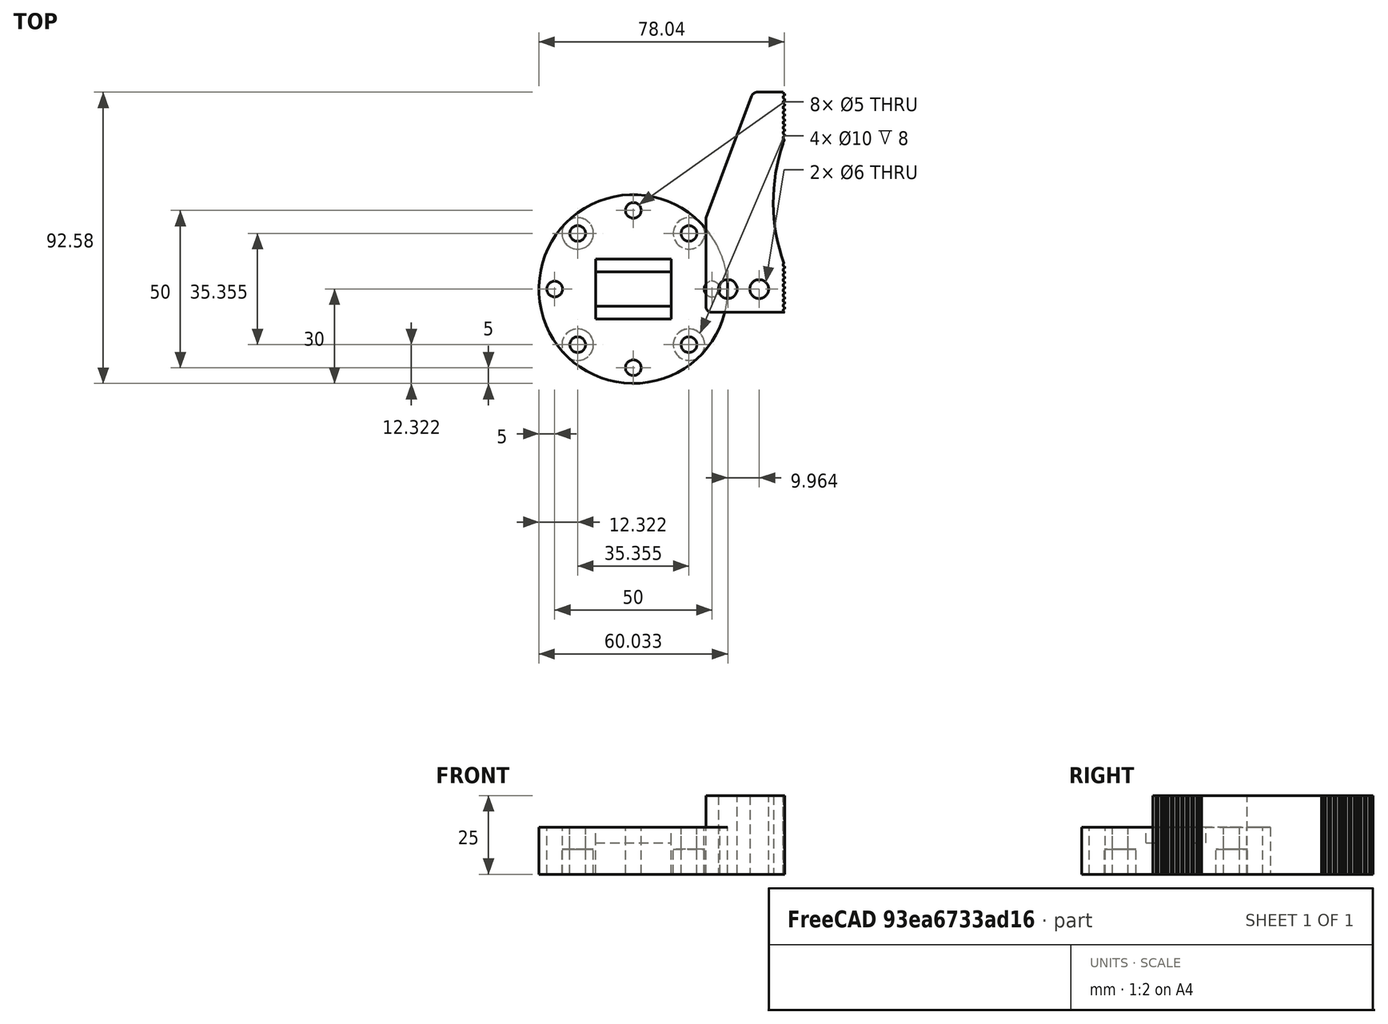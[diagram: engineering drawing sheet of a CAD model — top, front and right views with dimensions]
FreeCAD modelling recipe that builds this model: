
FCSTD DOCUMENT  (FreeCAD 0.16R6712 (Git))
Label: Garra
License: All rights reserved
LicenseURL: http://en.wikipedia.org/wiki/All_rights_reserved
objects: Part::Cylinder×5, Part::FeaturePython×5, Part::Cut×4, Sketcher::SketchObject×3, App::DocumentObjectGroup×3, PartDesign::Pad×2, Part::Fillet×2, Part::Box×1
note: 24 computed .brp shape members not serialized (recipe doc carries the construction recipe); baked Part::Feature solids carry a one-line shape summary decoded from their .brp

FEATURE [Sketcher::SketchObject] Sketch
  sketch-geometry (9):
    g0: LineSegment StartX=23.0433 StartY=-7.41801 StartZ=0 EndX=48.0433 EndY=-7.41801 EndZ=0
    g1: LineSegment StartX=23.0433 StartY=-7.41801 StartZ=0 EndX=23.0433 EndY=22.582 EndZ=0
    g2: LineSegment StartX=48.0433 StartY=-7.41801 StartZ=0 EndX=48.0433 EndY=7.58199 EndZ=0
    g3: LineSegment StartX=23.0433 StartY=22.582 StartZ=0 EndX=38.0433 EndY=62.582 EndZ=0
    g4: LineSegment StartX=38.0433 StartY=62.582 StartZ=0 EndX=48.0433 EndY=62.582 EndZ=0
    g5: LineSegment StartX=48.0433 StartY=62.582 StartZ=0 EndX=48.0433 EndY=47.582 EndZ=0
    g6: ArcOfCircle CenterX=102.486 CenterY=27.582 CenterZ=0 NormalX=0 NormalY=0 NormalZ=1 Radius=58 StartAngle=2.78954 EndAngle=3.49365
    g7: Circle CenterX=30.0326 CenterY=0 CenterZ=0 NormalX=0 NormalY=0 NormalZ=1 Radius=3
    g8: Circle CenterX=39.997 CenterY=0 CenterZ=0 NormalX=0 NormalY=0 NormalZ=1 Radius=3
  constraints (24):
    c: Horizontal(g0)
    c: Coincident(g1,g0)
    c: Vertical(g1)
    c: Coincident(g2,g0)
    c: Vertical(g2)
    c: DistanceY(g1,g1) = 30
    c: DistanceX(g0,g0) = 25
    c: DistanceY(g2,g2) = 15
    c: Coincident(g3,g1)
    c: DistanceY(g1,g3) = 40
    c: DistanceX(g1,g3) = 15
    c: Coincident(g4,g3)
    c: Horizontal(g4)
    c: DistanceX(g4,g4) = 10
    c: Coincident(g5,g4)
    c: Vertical(g5)
    c: DistanceY(g5,g5) = 15
    c: Coincident(g6,g2)
    c: Coincident(g6,g5)
    c: PointOnObject(g7,g-1)
    c: PointOnObject(g8,g-1)
    c: Equal(g7,g8)
    c: Radius(g7) = 3
    c: Radius(g6) = 58
FEATURE [PartDesign::Pad] Pad
  Length = 25
  Length2 = 100
  Sketch = -> Sketch
  Type = 0
FEATURE [Part::Cylinder] Cylinder  label="Cilindro"
  Angle = 360
  Height = 34
  Placement = pos=(48,-6.83755,0) rot=(0,0,1;0rad)
  Radius = 0.5
FEATURE [Part::FeaturePython] PathArray  # WARN: FeaturePython — macro-defined, semantics opaque (R4)
  Align = false
  Base = -> Cylinder
  Count = 45
  Xlate = (0,0,0)
FEATURE [Part::Cut] Cut
  Base = -> Pad
  Tool = -> PathArray
FEATURE [Part::Fillet] Fillet
  Base = -> Cut
  Edges = 1 edges r=2: [Edge1]
FEATURE [Part::Fillet] Fillet001
  Base = -> Fillet
  Edges = 1 edges r=2: [Edge105]
FEATURE [App::DocumentObjectGroup] Grupo  label="Garra"
  Group = -> [Fillet,Fillet001]
FEATURE [Sketcher::SketchObject] Sketch001
  sketch-geometry (6):
    g0: Circle CenterX=0 CenterY=0 CenterZ=0 NormalX=0 NormalY=0 NormalZ=1 Radius=30
    g1: Circle [constr] CenterX=0 CenterY=0 CenterZ=0 NormalX=0 NormalY=0 NormalZ=1 Radius=25
    g2: LineSegment StartX=-12 StartY=5.5 StartZ=0 EndX=12 EndY=5.5 EndZ=0
    g3: LineSegment StartX=12 StartY=5.5 StartZ=0 EndX=12 EndY=-5.5 EndZ=0
    g4: LineSegment StartX=12 StartY=-5.5 StartZ=0 EndX=-12 EndY=-5.5 EndZ=0
    g5: LineSegment StartX=-12 StartY=-5.5 StartZ=0 EndX=-12 EndY=5.5 EndZ=0
  constraints (16):
    c: Coincident(g0,g-1)
    c: Radius(g0) = 30
    c: Coincident(g1,g-1)
    c: Radius(g1) = 25
    c: Coincident(g2,g3)
    c: Coincident(g3,g4)
    c: Coincident(g4,g5)
    c: Coincident(g5,g2)
    c: Horizontal(g2)
    c: Horizontal(g4)
    c: Vertical(g3)
    c: Vertical(g5)
    c: DistanceY(g5,g5) = 11
    c: DistanceX(g2,g2) = 24
    c: Symmetric(g2,g2,g-2)
    c: Symmetric(g2,g4,g-1)
FEATURE [Part::Cylinder] Cylinder001  label="Cilindro001"
  Angle = 360
  Height = 15
  Placement = pos=(0,-25,0) rot=(0,0,1;0rad)
  Radius = 2.5
FEATURE [PartDesign::Pad] Pad001
  Length = 15
  Length2 = 100
  Sketch = -> Sketch001
  Type = 0
FEATURE [Part::FeaturePython] PathArray001  label="Taladro"  # WARN: FeaturePython — macro-defined, semantics opaque (R4)
  Align = false
  Base = -> Cylinder001
  Count = 8
  Xlate = (0,0,0)
FEATURE [Part::Cut] Cut001
  Base = -> Pad001
  Tool = -> PathArray001
FEATURE [Part::Cylinder] Cylinder002  label="Cilindro002"
  Angle = 360
  Height = 8
  Placement = pos=(17.67,17.67,0) rot=(0,0,1;0rad)
  Radius = 5
FEATURE [Part::FeaturePython] PathArray002  label="Taladrogrande"  # WARN: FeaturePython — macro-defined, semantics opaque (R4)
  Align = false
  Base = -> Cylinder002
  Count = 4
  Placement = pos=(0,0,0) rot=(0,0,1;0.785398rad)
  Xlate = (0,0,0)
FEATURE [Part::Cut] Cut002
  Base = -> Cut001
  Tool = -> PathArray002
FEATURE [Part::Box] Box  label="Cubo"
  Height = 10
  Length = 24
  Placement = pos=(-12,-9.5,10) rot=(0,0,1;0rad)
  Width = 19
FEATURE [Part::Cut] Cut003
  Base = -> Cut002
  Tool = -> Box
FEATURE [App::DocumentObjectGroup] Grupo001  label="Basecircularbaja"
  Group = -> [Cut003]
FEATURE [Sketcher::SketchObject] Sketch002
  sketch-geometry (10):
    g0: Circle CenterX=0 CenterY=0 CenterZ=0 NormalX=0 NormalY=0 NormalZ=1 Radius=30
    g1: Circle [constr] CenterX=0 CenterY=0 CenterZ=0 NormalX=0 NormalY=0 NormalZ=1 Radius=25
    g2: LineSegment StartX=-12 StartY=9.5 StartZ=0 EndX=12 EndY=9.5 EndZ=0
    g3: LineSegment StartX=12 StartY=9.5 StartZ=0 EndX=12 EndY=-9.5 EndZ=0
    g4: LineSegment StartX=12 StartY=-9.5 StartZ=0 EndX=-12 EndY=-9.5 EndZ=0
    g5: LineSegment StartX=-12 StartY=-9.5 StartZ=0 EndX=-12 EndY=9.5 EndZ=0
    g6: Circle CenterX=0 CenterY=0 CenterZ=0 NormalX=0 NormalY=0 NormalZ=1 Radius=5
    g7: LineSegment [constr] StartX=0 StartY=0 StartZ=0 EndX=-7 EndY=0 EndZ=0
    g8: Circle CenterX=-7 CenterY=0 CenterZ=0 NormalX=0 NormalY=0 NormalZ=1 Radius=1.5
    g9: Circle CenterX=7 CenterY=0 CenterZ=0 NormalX=0 NormalY=0 NormalZ=1 Radius=1.5
  constraints (25):
    c: Coincident(g0,g-1)
    c: Radius(g0) = 30
    c: Coincident(g1,g-1)
    c: Radius(g1) = 25
    c: Coincident(g2,g3)
    c: Coincident(g3,g4)
    c: Coincident(g4,g5)
    c: Coincident(g5,g2)
    c: Horizontal(g2)
    c: Horizontal(g4)
    c: Vertical(g3)
    c: Vertical(g5)
    c: DistanceY(g5,g5) = 19
    c: DistanceX(g2,g2) = 24
    c: Symmetric(g2,g2,g-2)
    c: Symmetric(g2,g4,g-1)
    c: Coincident(g6,g-1)
    c: Radius(g6) = 5
    c: Coincident(g7,g-1)
    c: Horizontal(g7)
    c: DistanceX(g7,g7) = 7
    c: Radius(g8) = 1.5
    c: Equal(g8,g9) = 1.5
    c: Coincident(g8,g7)
    c: Symmetric(g7,g9,g-2)
FEATURE [Part::Cylinder] Cylinder003  label="Cilindro003"
  Angle = 360
  Height = 15
  Placement = pos=(0,-25,0) rot=(0,0,1;0rad)
  Radius = 2.5
FEATURE [Part::FeaturePython] PathArray003  label="Taladro001"  # WARN: FeaturePython — macro-defined, semantics opaque (R4)
  Align = false
  Base = -> Cylinder003
  Count = 8
  Xlate = (0,0,0)
FEATURE [Part::Cylinder] Cylinder004  label="Cilindro004"
  Angle = 360
  Height = 8
  Placement = pos=(17.67,17.67,0) rot=(0,0,1;0rad)
  Radius = 5
FEATURE [Part::FeaturePython] PathArray004  label="Taladrogrande001"  # WARN: FeaturePython — macro-defined, semantics opaque (R4)
  Align = false
  Base = -> Cylinder004
  Count = 4
  Placement = pos=(0,0,0) rot=(0,0,1;0.785398rad)
  Xlate = (0,0,0)
FEATURE [App::DocumentObjectGroup] Grupo002
  Group = -> [PathArray003,PathArray004]
